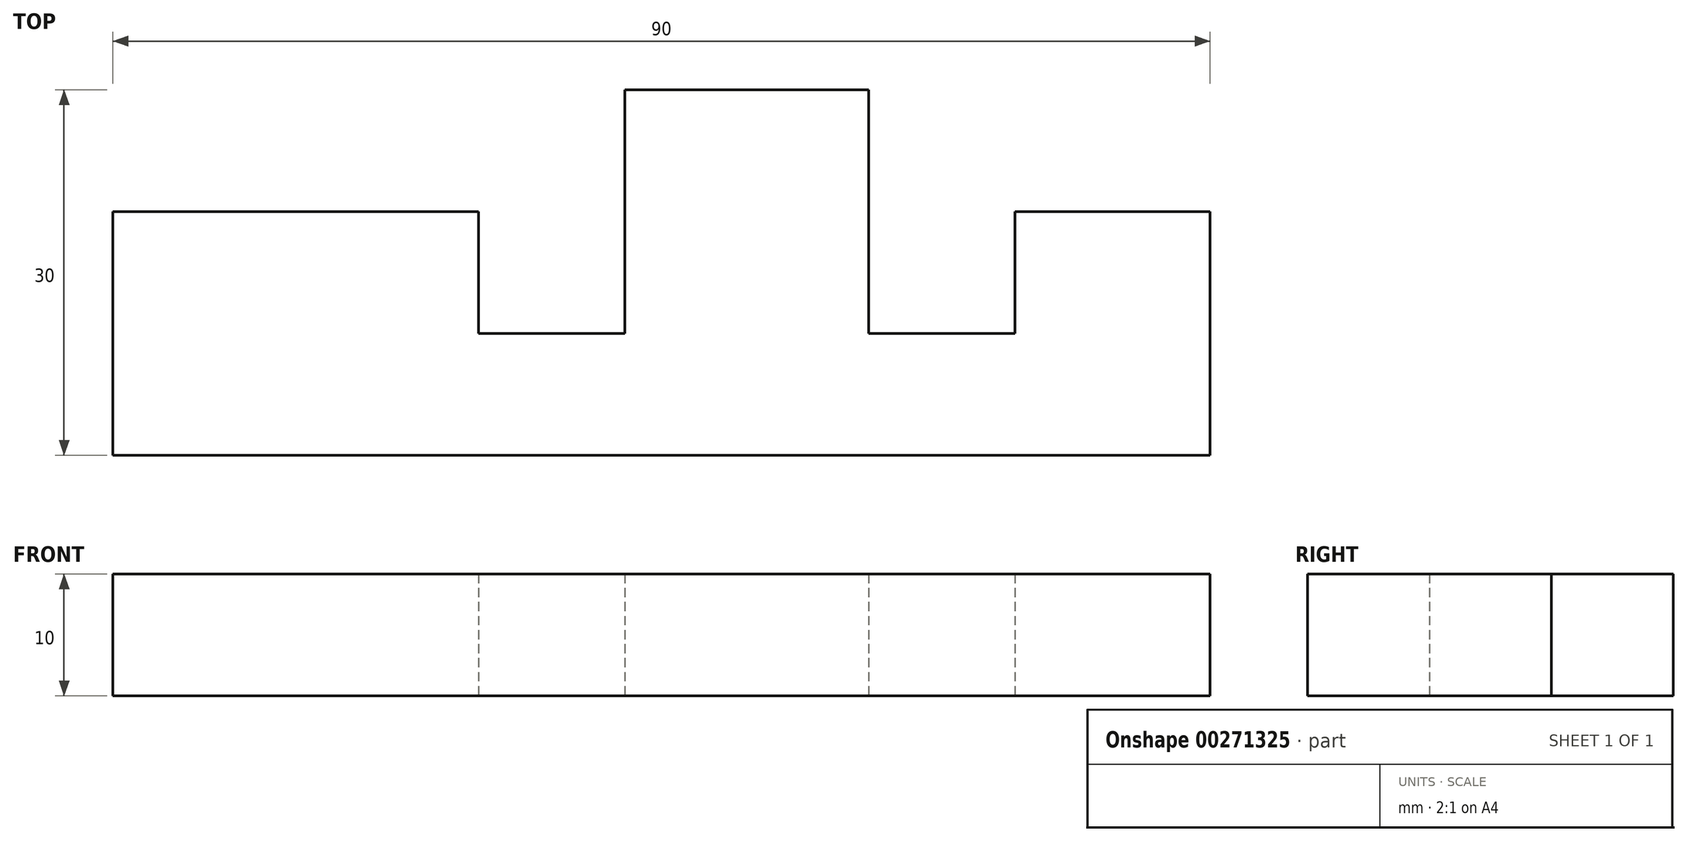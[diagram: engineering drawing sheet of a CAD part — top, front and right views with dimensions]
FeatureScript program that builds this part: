
annotation { "Feature Type Name" : "Feature", "Feature Type Description" : "" }
export const myFeature = defineFeature(function(context is Context, id is Id, definition is map)
    precondition{}
    {
        {
            var Q0;
            Q0=qCreatedBy(makeId("Top.planeOp"),FACE);
            var sketch = newSketch(context, id + "F0", { "sketchPlane" : qUnion([Q0])});
            skLineSegment(sketch, "E0", {"start": v(0, 0) * mm, "end": v(90, 0) * mm});
            skLineSegment(sketch, "E1", {"start": v(90, 0) * mm, "end": v(90, 20) * mm});
            skLineSegment(sketch, "E2", {"start": v(90, 20) * mm, "end": v(74, 20) * mm});
            skLineSegment(sketch, "E3", {"start": v(74, 20) * mm, "end": v(74, 10) * mm});
            skLineSegment(sketch, "E4", {"start": v(74, 10) * mm, "end": v(62, 10) * mm});
            skLineSegment(sketch, "E5", {"start": v(62, 10) * mm, "end": v(62, 30) * mm});
            skLineSegment(sketch, "E6", {"start": v(62, 30) * mm, "end": v(42, 30) * mm});
            skLineSegment(sketch, "E7", {"start": v(42, 30) * mm, "end": v(42, 10) * mm});
            skLineSegment(sketch, "E8", {"start": v(42, 10) * mm, "end": v(30, 10) * mm});
            skLineSegment(sketch, "E9", {"start": v(30, 10) * mm, "end": v(30, 20) * mm});
            skLineSegment(sketch, "E10", {"start": v(30, 20) * mm, "end": v(0, 20) * mm});
            skLineSegment(sketch, "E11", {"start": v(0, 20) * mm, "end": v(0, 0) * mm});
            skSolve(sketch);
        }
        {
            var Q0;
            Q0 = qSketchRegion(id + "F0", true);
            extrude(context, id + "F1", {"entities" : qUnion([Q0]), "depth" : 10 * mm});
        }
    });
